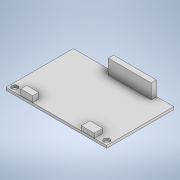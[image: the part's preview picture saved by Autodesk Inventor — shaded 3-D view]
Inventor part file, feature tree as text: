
AUTODESK INVENTOR PART (.ipt)
format: ipt  version: 2022.2 (Build 262287000, 287)  size: 138,752 bytes
history: native  units: in
note: dims shown in document units (in); Inventor stores cm internally (conversion verified against a paired STEP export)
features: extrude x4, sketch x3, other x1
ambient origin geometry x8: Origin, YZ Plane, XZ Plane, XY Plane, X Axis, Y Axis, Z Axis, Center Point
bodies: Solid1 (feature_tree)
feature tree (8):
  extrude  "Base Extrusion"  Depth=1.5394in
  extrude  "MicroUSB slot"  Depth=0.0984in
  extrude  "Reset Button"  Depth=0.0984in
  extrude  "Extrusion4"  Depth=0.0984in
  other  "Base Board"
  sketch  "Sketch2"  dims[d0=2.3031in d1=1.5394in]
  sketch  "Sketch3"  dims[d6=0.1382in d8=0.1382in d10=0.0984in]
  sketch  "Sketch4"  dims[d11=0.0984in d12=0.0984in d13=0.0984in d14=0.0591in d15=0.0in d16=0.2992in d17=0.1969in d19=0.0984in d20=0.0in d21=0.2854in d22=0.2756in d23=0.1378in d24=0.3287in d25=0.1319in d26=0.0in d27=0.9843in d28=0.1181in d29=0.3937in d30=0.3366in d31=0.0in]
